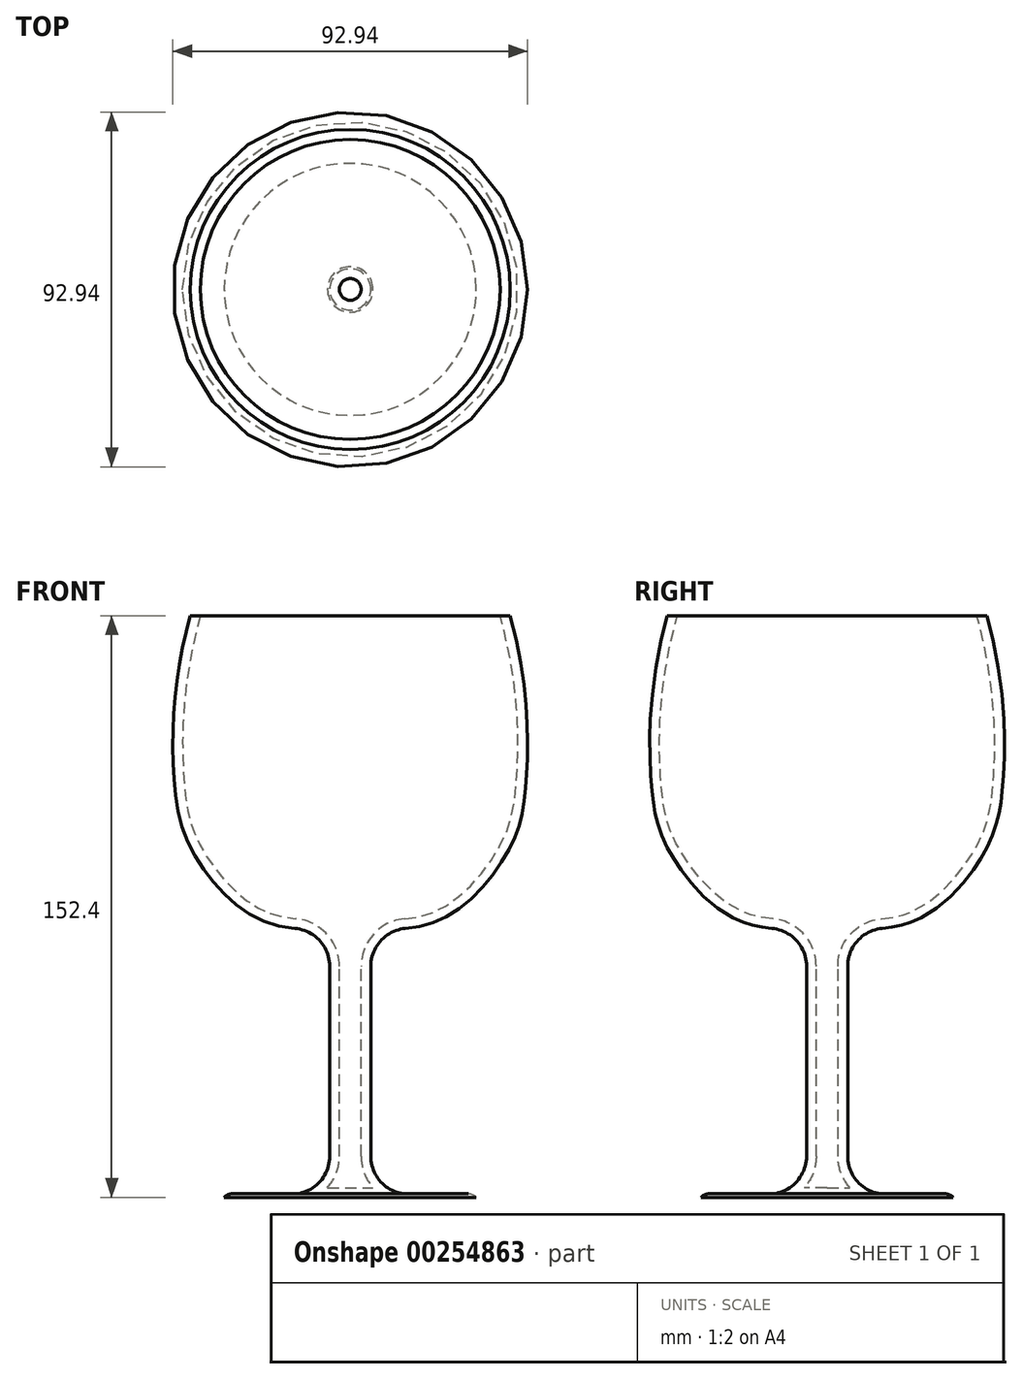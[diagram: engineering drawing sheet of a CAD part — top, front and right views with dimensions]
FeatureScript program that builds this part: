
annotation { "Feature Type Name" : "Feature", "Feature Type Description" : "" }
export const myFeature = defineFeature(function(context is Context, id is Id, definition is map)
    precondition{}
    {
        {
            var Q0;
            Q0=qCreatedBy(makeId("Front.planeOp"),FACE);
            var sketch = newSketch(context, id + "F0", { "sketchPlane" : qUnion([Q0])});
            skLineSegment(sketch, "E0", {"start": v(0, 85.39) * mm, "end": v(0, -67.01) * mm, "construction": true});
            skLineSegment(sketch, "E1", {"start": v(0, -67.01) * mm, "end": v(-33.02, -67.01) * mm});
            skLineSegment(sketch, "E2", {"start": v(0, 85.39) * mm, "end": v(-41.91, 85.39) * mm});
            skFitSpline(sketch, "E3", {"points": [v(-41.91, 85.39) * mm, v(-46.13, 42.44) * mm, v(-41.8, 24.52) * mm, v(-23.94, 5.84) * mm, v(0, 3.47) * mm], "startDerivative": vector(-46.83, -172.95) * mm, "endDerivative": vector(114.75, 1.73) * mm});
            skFitSpline(sketch, "E4", {"points": [v(-33.02, -67.01) * mm, v(-32.34, -66.45) * mm, v(-31.24, -66.1) * mm, v(-30.2, -66.1) * mm, v(0, -66.17) * mm], "startDerivative": vector(5.28, 5.57) * mm, "endDerivative": vector(63.4, 0.08) * mm});
            skLineSegment(sketch, "E5", {"start": v(-5.4, 3.34) * mm, "end": v(-5.4, -67.01) * mm});
            skLineSegment(sketch, "E6", {"start": v(0, 85.39) * mm, "end": v(0, -67.01) * mm});
            skSolve(sketch);
        }
        {
            var Q0;
            {var subQ0=sQuery(id+"F0.wireOp",EDGE,"E6");var subQ1=sQuery(id+"F0.wireOp",EDGE,"E3");var subQ2=makeQuery(id+"F0.imprint","INTERSECT",VERTEX,{"derivedFrom":[subQ1,subQ0]});Q0=makeQuery(id+"F0.imprint","IMPRINT",FACE,{"disambiguationData":[TD([[makeQuery(id+"F0.imprint","IMPRINT",EDGE,{"disambiguationData":[TD([[subQ2,1.0]])],"derivedFrom":subQ1}),-1.0]])]});}
            var Q1;
            {var subQ0=sQuery(id+"F0.wireOp",EDGE,"E2");Q1=makeQuery(id+"F0.imprint","IMPRINT",FACE,{"disambiguationData":[TD([[makeQuery(id+"F0.imprint","IMPRINT",EDGE,{"derivedFrom":subQ0}),1.0]])]});}
            var Q2;
            {var subQ0=sQuery(id+"F0.wireOp",EDGE,"E4");var subQ1=sQuery(id+"F0.wireOp",EDGE,"E1");var subQ2=makeQuery(id+"F0.imprint","INTERSECT",VERTEX,{"derivedFrom":[subQ1,subQ0]});Q2=makeQuery(id+"F0.imprint","IMPRINT",FACE,{"disambiguationData":[TD([[makeQuery(id+"F0.imprint","IMPRINT",EDGE,{"disambiguationData":[TD([[subQ2,1.0]])],"derivedFrom":subQ1}),-1.0]])]});}
            var Q3;
            {var subQ0=sQuery(id+"F0.wireOp",EDGE,"E6");var subQ1=sQuery(id+"F0.wireOp",EDGE,"E1");var subQ2=makeQuery(id+"F0.imprint","INTERSECT",VERTEX,{"derivedFrom":[subQ1,subQ0]});Q3=makeQuery(id+"F0.imprint","IMPRINT",FACE,{"disambiguationData":[TD([[makeQuery(id+"F0.imprint","IMPRINT",EDGE,{"disambiguationData":[TD([[subQ2,-1.0]])],"derivedFrom":subQ1}),-1.0]])]});}
            var Q4;
            Q4=sQuery(id+"F0.wireOp",EDGE,"E6");
            revolve(context, id + "F1", {"entities" : qUnion([Q0, Q1, Q2, Q3]), "axis" : qUnion([Q4]), "revolveType" : RevolveType.FULL});
        }
        {
            var Q0;
            Q0=makeQuery(id+"F1.opRevolve","SWEPT_FACE",FACE,{"disambiguationData":[OSD([sQuery(id+"F0.wireOp",EDGE,"E5")])]});
            fillet(context, id + "F2", {"entities" : qUnion([Q0]), "radius" : 9.95 * mm, "tangentPropagation" : true, "allowEdgeOverflow" : false});
        }
        {
            var Q0;
            Q0=makeQuery(id+"F1.opRevolve","SWEPT_FACE",FACE,{"disambiguationData":[OSD([sQuery(id+"F0.wireOp",EDGE,"E2")])]});
            shell(context, id + "F3", {"entities" : qUnion([Q0]), "thickness" : 2.54 * mm});
        }
    });
